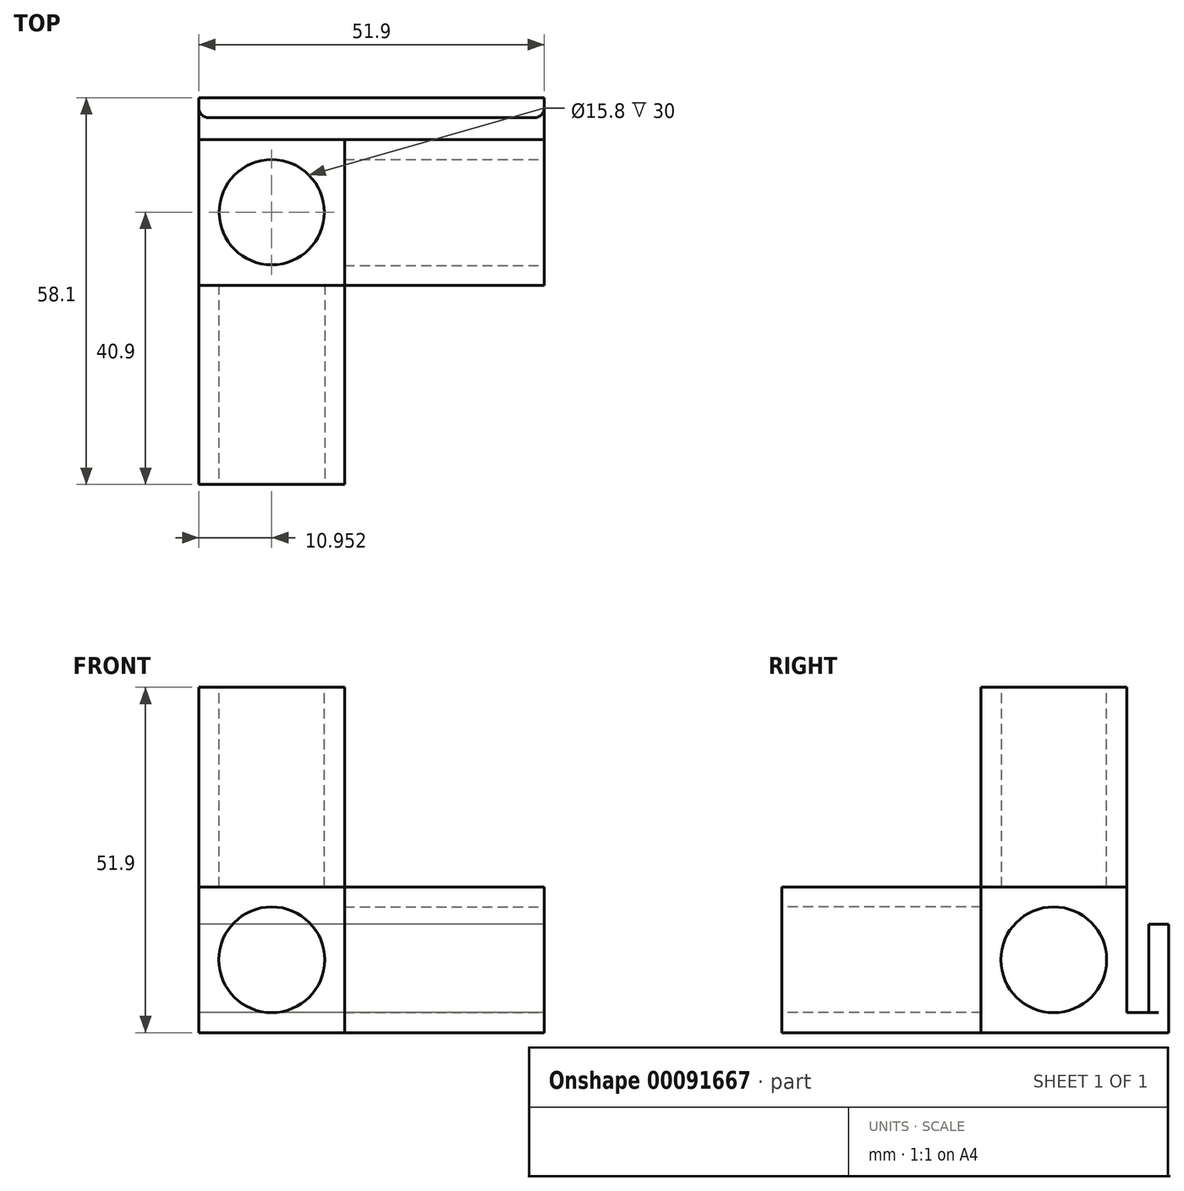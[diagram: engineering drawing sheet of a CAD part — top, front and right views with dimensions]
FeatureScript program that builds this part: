
annotation { "Feature Type Name" : "Feature", "Feature Type Description" : "" }
export const myFeature = defineFeature(function(context is Context, id is Id, definition is map)
    precondition{}
    {
        {
            var Q0;
            Q0=qCreatedBy(makeId("Front.planeOp"),FACE);
            var sketch = newSketch(context, id + "F0", { "sketchPlane" : qUnion([Q0])});
            skLineSegment(sketch, "E0.bottom", {"start": v(-42.3, 45.9) * mm, "end": v(-26.4, 45.9) * mm});
            skLineSegment(sketch, "E0.top", {"start": v(-42.3, 0) * mm, "end": v(-26.4, 0) * mm});
            skLineSegment(sketch, "E0.left", {"start": v(-42.3, 45.9) * mm, "end": v(-42.3, 0) * mm});
            skLineSegment(sketch, "E0.right", {"start": v(-26.4, 45.9) * mm, "end": v(-26.4, 15.9) * mm});
            skLineSegment(sketch, "E1.top", {"start": v(-42.3, 15.9) * mm, "end": v(-26.4, 15.9) * mm});
            skLineSegment(sketch, "E1.left", {"start": v(-42.3, 0) * mm, "end": v(-42.3, 15.9) * mm});
            skLineSegment(sketch, "E1.right", {"start": v(3.6, 0) * mm, "end": v(3.6, 15.9) * mm});
            skLineSegment(sketch, "E2", {"start": v(-26.4, 15.9) * mm, "end": v(-26.4, 0) * mm});
            skLineSegment(sketch, "E3", {"start": v(-26.4, 15.9) * mm, "end": v(3.6, 15.9) * mm});
            skLineSegment(sketch, "E4", {"start": v(-26.4, 0) * mm, "end": v(-26.4, 0) * mm});
            skLineSegment(sketch, "E5", {"start": v(-42.3, 15.9) * mm, "end": v(-42.3, 15.9) * mm});
            skLineSegment(sketch, "E6", {"start": v(-26.4, 0) * mm, "end": v(3.6, 0) * mm});
            skLineSegment(sketch, "E7.0", {"start": v(-45.3, 48.9) * mm, "end": v(-45.3, -3) * mm});
            skLineSegment(sketch, "E7.1", {"start": v(-45.3, -3) * mm, "end": v(-23.4, -3) * mm});
            skLineSegment(sketch, "E7.2", {"start": v(-23.4, 48.9) * mm, "end": v(-23.4, 18.9) * mm});
            skLineSegment(sketch, "E7.3", {"start": v(-23.4, 18.9) * mm, "end": v(6.6, 18.9) * mm});
            skLineSegment(sketch, "E7.4", {"start": v(6.6, -3) * mm, "end": v(6.6, 18.9) * mm});
            skLineSegment(sketch, "E7.5", {"start": v(-45.3, 48.9) * mm, "end": v(-23.4, 48.9) * mm});
            skLineSegment(sketch, "E7.6", {"start": v(-23.4, -3) * mm, "end": v(6.6, -3) * mm});
            skPoint(sketch, "E8", {"position": v(-34.36, 7.95) * mm});
            skPoint(sketch, "E8.positionSnap0", {"position": v(-26.4, 7.95) * mm});
            skPoint(sketch, "E8.positionSnap1", {"position": v(-34.36, 15.9) * mm});
            skCircle(sketch, "E9", {"center": v(-34.36, 7.95) * mm, "radius": 7.95 * mm});
            skLineSegment(sketch, "E10", {"start": v(-23.4, 18.9) * mm, "end": v(-45.3, 18.9) * mm});
            skLineSegment(sketch, "E11", {"start": v(-23.4, 18.9) * mm, "end": v(-23.4, -3) * mm});
            skSolve(sketch);
        }
        {
            var Q0;
            {var subQ1=sQuery(id+"F0.wireOp",EDGE,"E1.top");var subQ3=sQuery(id+"F0.wireOp",EDGE,"E9");var subQ4=makeQuery(id+"F0.imprint","INTERSECT",VERTEX,{"derivedFrom":[subQ1,subQ3]});Q0=makeQuery(id+"F0.imprint","IMPRINT",FACE,{"disambiguationData":[TD([[makeQuery(id+"F0.imprint","IMPRINT",EDGE,{"disambiguationData":[TD([[subQ4,-1.0]])],"derivedFrom":subQ3}),-1.0]])]});}
            var Q1;
            {var subQ0=sQuery(id+"F0.wireOp",EDGE,"E9");var subQ1=makeQuery(id+"F0.imprint","INTERSECT",VERTEX,{"derivedFrom":[sQuery(id+"F0.wireOp",EDGE,"E1.top"),subQ0]});Q1=makeQuery(id+"F0.imprint","IMPRINT",FACE,{"disambiguationData":[TD([[makeQuery(id+"F0.imprint","IMPRINT",EDGE,{"disambiguationData":[TD([[subQ1,1.0]])],"derivedFrom":subQ0}),1.0]])]});}
            var Q2;
            {var subQ5=sQuery(id+"F0.wireOp",EDGE,"E0.bottom");Q2=makeQuery(id+"F0.imprint","IMPRINT",FACE,{"disambiguationData":[TD([[makeQuery(id+"F0.imprint","IMPRINT",EDGE,{"derivedFrom":subQ5}),1.0]])]});}
            var Q3;
            {var subQ0=sQuery(id+"F0.wireOp",EDGE,"E1.right");Q3=makeQuery(id+"F0.imprint","IMPRINT",FACE,{"disambiguationData":[TD([[makeQuery(id+"F0.imprint","IMPRINT",EDGE,{"derivedFrom":subQ0}),1.0]])]});}
            var Q4;
            {var subQ0=sQuery(id+"F0.wireOp",EDGE,"E0.bottom");Q4=makeQuery(id+"F0.imprint","IMPRINT",FACE,{"disambiguationData":[TD([[makeQuery(id+"F0.imprint","IMPRINT",EDGE,{"derivedFrom":subQ0}),-1.0]])]});}
            var Q5;
            {var subQ0=sQuery(id+"F0.wireOp",EDGE,"E1.left");var subQ1=sQuery(id+"F0.wireOp",EDGE,"E0.top");var subQ2=makeQuery(id+"F0.imprint","INTERSECT",VERTEX,{"derivedFrom":[subQ1,subQ0]});Q5=makeQuery(id+"F0.imprint","IMPRINT",FACE,{"disambiguationData":[TD([[makeQuery(id+"F0.imprint","IMPRINT",EDGE,{"disambiguationData":[TD([[subQ2,-1.0]])],"derivedFrom":subQ1}),1.0]])]});}
            var Q6;
            {var subQ1=sQuery(id+"F0.wireOp",EDGE,"E0.top");var subQ3=sQuery(id+"F0.wireOp",EDGE,"E9");var subQ4=makeQuery(id+"F0.imprint","INTERSECT",VERTEX,{"derivedFrom":[subQ1,subQ3]});Q6=makeQuery(id+"F0.imprint","IMPRINT",FACE,{"disambiguationData":[TD([[makeQuery(id+"F0.imprint","IMPRINT",EDGE,{"disambiguationData":[TD([[subQ4,-1.0]])],"derivedFrom":subQ3}),-1.0]])]});}
            var Q7;
            {var subQ1=sQuery(id+"F0.wireOp",EDGE,"E1.top");var subQ3=sQuery(id+"F0.wireOp",EDGE,"E9");var subQ4=makeQuery(id+"F0.imprint","INTERSECT",VERTEX,{"derivedFrom":[subQ1,subQ3]});Q7=makeQuery(id+"F0.imprint","IMPRINT",FACE,{"disambiguationData":[TD([[makeQuery(id+"F0.imprint","IMPRINT",EDGE,{"disambiguationData":[TD([[subQ4,1.0]])],"derivedFrom":subQ3}),-1.0]])]});}
            var Q8;
            {var subQ5=sQuery(id+"F0.wireOp",EDGE,"E1.right");Q8=makeQuery(id+"F0.imprint","IMPRINT",FACE,{"disambiguationData":[TD([[makeQuery(id+"F0.imprint","IMPRINT",EDGE,{"derivedFrom":subQ5}),-1.0]])]});}
            var Q9;
            {var subQ4=sQuery(id+"F0.wireOp",EDGE,"E0.left");var subQ6=sQuery(id+"F0.wireOp",EDGE,"E10");var subQ8=makeQuery(id+"F0.imprint","INTERSECT",VERTEX,{"derivedFrom":[subQ4,subQ6]});Q9=makeQuery(id+"F0.imprint","IMPRINT",FACE,{"disambiguationData":[TD([[makeQuery(id+"F0.imprint","IMPRINT",EDGE,{"disambiguationData":[TD([[subQ8,1.0]])],"derivedFrom":subQ6}),1.0]])]});}
            var Q10;
            {var subQ3=sQuery(id+"F0.wireOp",EDGE,"E11");var subQ5=sQuery(id+"F0.wireOp",EDGE,"E3");var subQ8=makeQuery(id+"F0.imprint","INTERSECT",VERTEX,{"derivedFrom":[subQ5,subQ3]});Q10=makeQuery(id+"F0.imprint","IMPRINT",FACE,{"disambiguationData":[TD([[makeQuery(id+"F0.imprint","IMPRINT",EDGE,{"disambiguationData":[TD([[subQ8,-1.0]])],"derivedFrom":subQ3}),-1.0]])]});}
            var Q11;
            {var subQ14=sQuery(id+"F0.wireOp",EDGE,"E7.1");Q11=makeQuery(id+"F0.imprint","IMPRINT",FACE,{"disambiguationData":[TD([[makeQuery(id+"F0.imprint","IMPRINT",EDGE,{"derivedFrom":subQ14}),1.0]])]});}
            var Q12;
            {var subQ1=sQuery(id+"F0.wireOp",EDGE,"E0.right");var subQ3=sQuery(id+"F0.wireOp",EDGE,"E10");var subQ4=makeQuery(id+"F0.imprint","INTERSECT",VERTEX,{"derivedFrom":[subQ1,subQ3]});Q12=makeQuery(id+"F0.imprint","IMPRINT",FACE,{"disambiguationData":[TD([[makeQuery(id+"F0.imprint","IMPRINT",EDGE,{"disambiguationData":[TD([[subQ4,-1.0]])],"derivedFrom":subQ1}),1.0]])]});}
            extrude(context, id + "F1", {"entities" : qUnion([Q0, Q1, Q2, Q3, Q4, Q5, Q6, Q7, Q8, Q9, Q10, Q11, Q12]), "depth" : (15.9 + 6) * mm});
        }
        {
            var Q0;
            {var subQ14=sQuery(id+"F0.wireOp",EDGE,"E7.1");Q0=makeQuery(id+"F0.imprint","IMPRINT",FACE,{"disambiguationData":[TD([[makeQuery(id+"F0.imprint","IMPRINT",EDGE,{"derivedFrom":subQ14}),1.0]])]});}
            var Q1;
            {var subQ0=sQuery(id+"F0.wireOp",EDGE,"E9");var subQ1=makeQuery(id+"F0.imprint","INTERSECT",VERTEX,{"derivedFrom":[sQuery(id+"F0.wireOp",EDGE,"E1.top"),subQ0]});Q1=makeQuery(id+"F0.imprint","IMPRINT",FACE,{"disambiguationData":[TD([[makeQuery(id+"F0.imprint","IMPRINT",EDGE,{"disambiguationData":[TD([[subQ1,1.0]])],"derivedFrom":subQ0}),1.0]])]});}
            var Q2;
            {var subQ4=sQuery(id+"F0.wireOp",EDGE,"E0.left");var subQ6=sQuery(id+"F0.wireOp",EDGE,"E10");var subQ8=makeQuery(id+"F0.imprint","INTERSECT",VERTEX,{"derivedFrom":[subQ4,subQ6]});Q2=makeQuery(id+"F0.imprint","IMPRINT",FACE,{"disambiguationData":[TD([[makeQuery(id+"F0.imprint","IMPRINT",EDGE,{"disambiguationData":[TD([[subQ8,1.0]])],"derivedFrom":subQ6}),1.0]])]});}
            var Q3;
            {var subQ3=sQuery(id+"F0.wireOp",EDGE,"E11");var subQ5=sQuery(id+"F0.wireOp",EDGE,"E3");var subQ8=makeQuery(id+"F0.imprint","INTERSECT",VERTEX,{"derivedFrom":[subQ5,subQ3]});Q3=makeQuery(id+"F0.imprint","IMPRINT",FACE,{"disambiguationData":[TD([[makeQuery(id+"F0.imprint","IMPRINT",EDGE,{"disambiguationData":[TD([[subQ8,-1.0]])],"derivedFrom":subQ3}),-1.0]])]});}
            var Q4;
            {var subQ1=sQuery(id+"F0.wireOp",EDGE,"E0.right");var subQ3=sQuery(id+"F0.wireOp",EDGE,"E10");var subQ4=makeQuery(id+"F0.imprint","INTERSECT",VERTEX,{"derivedFrom":[subQ1,subQ3]});Q4=makeQuery(id+"F0.imprint","IMPRINT",FACE,{"disambiguationData":[TD([[makeQuery(id+"F0.imprint","IMPRINT",EDGE,{"disambiguationData":[TD([[subQ4,-1.0]])],"derivedFrom":subQ1}),1.0]])]});}
            var Q5;
            {var subQ1=sQuery(id+"F0.wireOp",EDGE,"E1.top");var subQ3=sQuery(id+"F0.wireOp",EDGE,"E9");var subQ4=makeQuery(id+"F0.imprint","INTERSECT",VERTEX,{"derivedFrom":[subQ1,subQ3]});Q5=makeQuery(id+"F0.imprint","IMPRINT",FACE,{"disambiguationData":[TD([[makeQuery(id+"F0.imprint","IMPRINT",EDGE,{"disambiguationData":[TD([[subQ4,1.0]])],"derivedFrom":subQ3}),-1.0]])]});}
            var Q6;
            {var subQ1=sQuery(id+"F0.wireOp",EDGE,"E1.top");var subQ3=sQuery(id+"F0.wireOp",EDGE,"E9");var subQ4=makeQuery(id+"F0.imprint","INTERSECT",VERTEX,{"derivedFrom":[subQ1,subQ3]});Q6=makeQuery(id+"F0.imprint","IMPRINT",FACE,{"disambiguationData":[TD([[makeQuery(id+"F0.imprint","IMPRINT",EDGE,{"disambiguationData":[TD([[subQ4,-1.0]])],"derivedFrom":subQ3}),-1.0]])]});}
            var Q7;
            {var subQ0=sQuery(id+"F0.wireOp",EDGE,"E1.left");var subQ1=sQuery(id+"F0.wireOp",EDGE,"E0.top");var subQ2=makeQuery(id+"F0.imprint","INTERSECT",VERTEX,{"derivedFrom":[subQ1,subQ0]});Q7=makeQuery(id+"F0.imprint","IMPRINT",FACE,{"disambiguationData":[TD([[makeQuery(id+"F0.imprint","IMPRINT",EDGE,{"disambiguationData":[TD([[subQ2,-1.0]])],"derivedFrom":subQ1}),1.0]])]});}
            var Q8;
            {var subQ1=sQuery(id+"F0.wireOp",EDGE,"E0.top");var subQ3=sQuery(id+"F0.wireOp",EDGE,"E9");var subQ4=makeQuery(id+"F0.imprint","INTERSECT",VERTEX,{"derivedFrom":[subQ1,subQ3]});Q8=makeQuery(id+"F0.imprint","IMPRINT",FACE,{"disambiguationData":[TD([[makeQuery(id+"F0.imprint","IMPRINT",EDGE,{"disambiguationData":[TD([[subQ4,-1.0]])],"derivedFrom":subQ3}),-1.0]])]});}
            extrude(context, id + "F2", {"entities" : qUnion([Q0, Q1, Q2, Q3, Q4, Q5, Q6, Q7, Q8]), "operationType" : NewBodyOperationType.ADD, "depth" : (15.8 + 6 + 30) * mm});
        }
        {
            var Q0;
            Q0=makeQuery(id+"F2.opExtrude","CAP_FACE",FACE,{"disambiguationData":[OSD([sQuery(id+"F0.wireOp",EDGE,"E7.0"),sQuery(id+"F0.wireOp",EDGE,"E7.1"),sQuery(id+"F0.wireOp",EDGE,"E10"),sQuery(id+"F0.wireOp",EDGE,"E11")])],"isStart":false});
            var sketch = newSketch(context, id + "F3", { "sketchPlane" : qUnion([Q0])});
            skCircle(sketch, "E12.0", {"center": v(-34.36, 7.95) * mm, "radius": 7.95 * mm});
            skSolve(sketch);
        }
        {
            var Q0;
            Q0=makeQuery(id+"F1.opExtrude","SWEPT_FACE",FACE,{"disambiguationData":[OSD([sQuery(id+"F0.wireOp",EDGE,"E7.5")])]});
            var sketch = newSketch(context, id + "F4", { "sketchPlane" : qUnion([Q0])});
            skPoint(sketch, "E13", {"position": v(-34.36, -3) * mm});
            skPoint(sketch, "E14", {"position": v(-26.4, -10.9) * mm});
            skPoint(sketch, "E15", {"position": v(-34.36, -10.9) * mm});
            skPoint(sketch, "E16", {"position": v(-62.98, 75) * mm});
            skPoint(sketch, "E17.orphan", {"position": v(-42.3, -3) * mm});
            skPoint(sketch, "E18.orphan", {"position": v(-26.4, -3) * mm});
            skPoint(sketch, "E19.orphan", {"position": v(-26.4, -18.8) * mm});
            skCircle(sketch, "E20", {"center": v(-34.36, -10.9) * mm, "radius": 7.9 * mm});
            skSolve(sketch);
        }
        {
            var Q0;
            Q0=makeQuery(id+"F1.opExtrude","SWEPT_FACE",FACE,{"disambiguationData":[OSD([sQuery(id+"F0.wireOp",EDGE,"E7.4")])]});
            var sketch = newSketch(context, id + "F5", { "sketchPlane" : qUnion([Q0])});
            skLineSegment(sketch, "E21.0", {"start": v(-18.9, 15.9) * mm, "end": v(-3, 15.9) * mm});
            skLineSegment(sketch, "E21.1", {"start": v(-18.9, 0) * mm, "end": v(-18.9, 15.9) * mm});
            skLineSegment(sketch, "E21.2", {"start": v(-18.9, 0) * mm, "end": v(-3, 0) * mm});
            skLineSegment(sketch, "E21.3", {"start": v(-3, 0) * mm, "end": v(-3, 15.9) * mm});
            skCircle(sketch, "E22", {"center": v(-10.95, 7.95) * mm, "radius": 7.95 * mm});
            skPoint(sketch, "E22.centerSnap0", {"position": v(-10.95, 0) * mm});
            skPoint(sketch, "E22.centerSnap1", {"position": v(-3, 7.95) * mm});
            skSolve(sketch);
        }
        {
            var Q0;
            Q0=makeQuery(id+"F3.imprint","IMPRINT",FACE,{"disambiguationData":[TD([[makeQuery(id+"F3.imprint","IMPRINT",EDGE,{"derivedFrom":sQuery(id+"F3.wireOp",EDGE,"E12.0")}),1.0]])]});
            extrude(context, id + "F6", {"entities" : qUnion([Q0]), "operationType" : NewBodyOperationType.REMOVE, "oppositeDirection" : true, "depth" : 30 * mm});
        }
        {
            var Q0;
            {var subQ0=sQuery(id+"F5.wireOp",EDGE,"E22");var subQ1=makeQuery(id+"F5.imprint","INTERSECT",VERTEX,{"derivedFrom":[sQuery(id+"F5.wireOp",EDGE,"E21.1"),subQ0]});Q0=makeQuery(id+"F5.imprint","IMPRINT",FACE,{"disambiguationData":[TD([[makeQuery(id+"F5.imprint","IMPRINT",EDGE,{"disambiguationData":[TD([[subQ1,1.0]])],"derivedFrom":subQ0}),1.0]])]});}
            extrude(context, id + "F7", {"entities" : qUnion([Q0]), "operationType" : NewBodyOperationType.REMOVE, "oppositeDirection" : true, "depth" : 30 * mm});
        }
        {
            var Q0;
            Q0=makeQuery(id+"F4.imprint","IMPRINT",FACE,{"disambiguationData":[TD([[makeQuery(id+"F4.imprint","IMPRINT",EDGE,{"derivedFrom":sQuery(id+"F4.wireOp",EDGE,"E20")}),1.0]])]});
            var Q1;
            Q1=sQuery(id+"F4.wireOp",EDGE,"E20");
            extrude(context, id + "F8", {"entities" : qUnion([Q0]), "operationType" : NewBodyOperationType.REMOVE, "surfaceEntities" : qUnion([Q1]), "oppositeDirection" : true, "depth" : 30 * mm});
        }
        {
            var Q0;
            {var subQ0=sQuery(id+"F0.wireOp",EDGE,"E7.0");Q0=makeQuery(id+"F2.boolean.opBoolean","MERGE",FACE,{"derivedFrom":[makeQuery(id+"F1.opExtrude","SWEPT_FACE",FACE,{"disambiguationData":[OSD([subQ0])]}),makeQuery(id+"F2.opExtrude","SWEPT_FACE",FACE,{"disambiguationData":[OSD([subQ0])]})]});}
            var sketch = newSketch(context, id + "F9", { "sketchPlane" : qUnion([Q0])});
            skLineSegment(sketch, "E23", {"start": v(0, -3) * mm, "end": v(-6.3, -3) * mm});
            skLineSegment(sketch, "E24", {"start": v(-6.3, -3) * mm, "end": v(-6.3, 13.3) * mm});
            skLineSegment(sketch, "E25", {"start": v(-6.3, 13.3) * mm, "end": v(-3.3, 13.3) * mm});
            skLineSegment(sketch, "E26", {"start": v(-3.3, 13.3) * mm, "end": v(-3.3, 0) * mm});
            skLineSegment(sketch, "E27", {"start": v(-3.3, 0) * mm, "end": v(0, 0) * mm});
            skSolve(sketch);
        }
        {
            var Q0;
            Q0 = qSketchRegion(id + "F9", true);
            var Q1;
            {var subQ0=sQuery(id+"F9.wireOp",EDGE,"E23");Q1=makeQuery(id+"F9.imprint","IMPRINT",FACE,{"disambiguationData":[TD([[makeQuery(id+"F9.imprint","IMPRINT",EDGE,{"derivedFrom":subQ0}),-1.0]])]});}
            extrude(context, id + "F10", {"entities" : qUnion([Q0, Q1]), "operationType" : NewBodyOperationType.ADD, "oppositeDirection" : true, "depth" : (6 + 15.9 + 30) * mm});
        }
        {
            var Q0;
            Q0=makeQuery(id+"F10.opExtrude","CAP_EDGE",EDGE,{"disambiguationData":[OSD([sQuery(id+"F9.wireOp",EDGE,"E26")])],"isStart":true});
            var Q1;
            Q1=makeQuery(id+"F10.opExtrude","CAP_EDGE",EDGE,{"disambiguationData":[OSD([sQuery(id+"F9.wireOp",EDGE,"E26")])],"isStart":false});
            fillet(context, id + "F11", {"entities" : qUnion([Q0, Q1]), "radius" : 1.5 * mm, "tangentPropagation" : true, "allowEdgeOverflow" : false});
        }
    });
